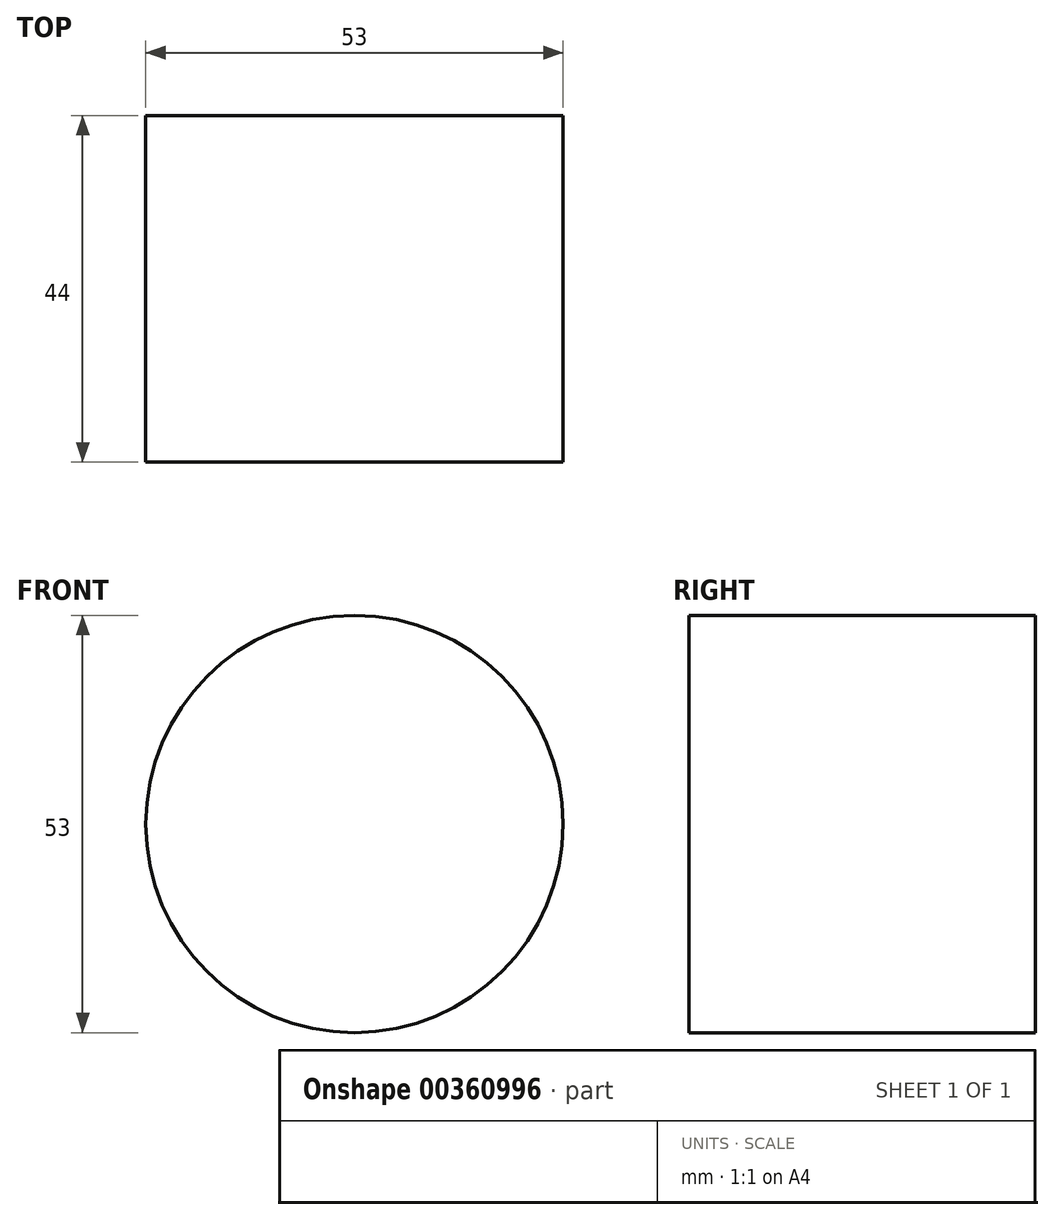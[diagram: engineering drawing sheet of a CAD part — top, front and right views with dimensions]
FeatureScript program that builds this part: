
annotation { "Feature Type Name" : "Feature", "Feature Type Description" : "" }
export const myFeature = defineFeature(function(context is Context, id is Id, definition is map)
    precondition{}
    {
        {
            var Q0;
            Q0=qCreatedBy(makeId("Front.planeOp"),FACE);
            var sketch = newSketch(context, id + "F0", { "sketchPlane" : qUnion([Q0])});
            skCircle(sketch, "E0", {"center": v(0, 0) * mm, "radius": 26.5 * mm});
            skSolve(sketch);
        }
        {
            var Q0;
            Q0 = qSketchRegion(id + "F0", true);
            extrude(context, id + "F1", {"entities" : qUnion([Q0]), "depth" : 44 * mm});
        }
    });
